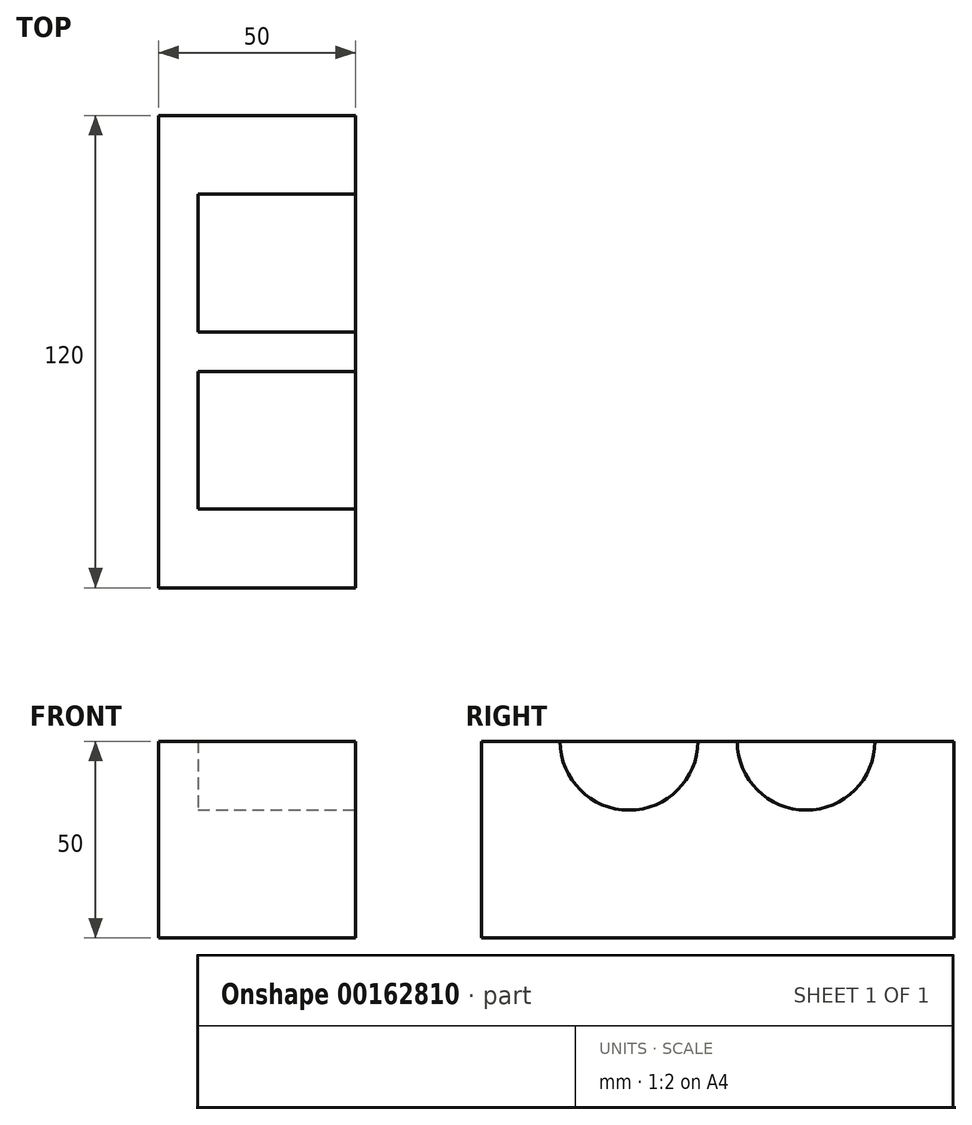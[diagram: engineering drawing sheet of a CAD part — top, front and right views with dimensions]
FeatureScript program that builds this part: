
annotation { "Feature Type Name" : "Feature", "Feature Type Description" : "" }
export const myFeature = defineFeature(function(context is Context, id is Id, definition is map)
    precondition{}
    {
        {
            var Q0;
            Q0=qCreatedBy(makeId("Top.planeOp"),FACE);
            var sketch = newSketch(context, id + "F0", { "sketchPlane" : qUnion([Q0])});
            skLineSegment(sketch, "E0.bottom", {"start": v(-25, 60) * mm, "end": v(25, 60) * mm});
            skLineSegment(sketch, "E0.top", {"start": v(-25, -60) * mm, "end": v(25, -60) * mm});
            skLineSegment(sketch, "E0.left", {"start": v(-25, 60) * mm, "end": v(-25, -60) * mm});
            skLineSegment(sketch, "E0.right", {"start": v(25, 60) * mm, "end": v(25, -60) * mm});
            skPoint(sketch, "E0.middle", {"position": v(0, 0) * mm});
            skSolve(sketch);
        }
        {
            var Q0;
            Q0 = qSketchRegion(id + "F0", true);
            extrude(context, id + "F1", {"entities" : qUnion([Q0]), "depth" : 50 * mm});
        }
        {
            var Q0;
            Q0=makeQuery(id+"F1.opExtrude","SWEPT_FACE",FACE,{"disambiguationData":[OSD([sQuery(id+"F0.wireOp",EDGE,"E0.right")])]});
            var sketch = newSketch(context, id + "F2", { "sketchPlane" : qUnion([Q0])});
            skCircle(sketch, "E1", {"center": v(-22.5, 50) * mm, "radius": 17.5 * mm});
            skCircle(sketch, "E2", {"center": v(22.5, 50) * mm, "radius": 17.5 * mm});
            skSolve(sketch);
        }
        {
            var Q0;
            Q0 = qSketchRegion(id + "F2", true);
            extrude(context, id + "F3", {"entities" : qUnion([Q0]), "operationType" : NewBodyOperationType.REMOVE, "oppositeDirection" : true, "depth" : 40 * mm});
        }
    });
